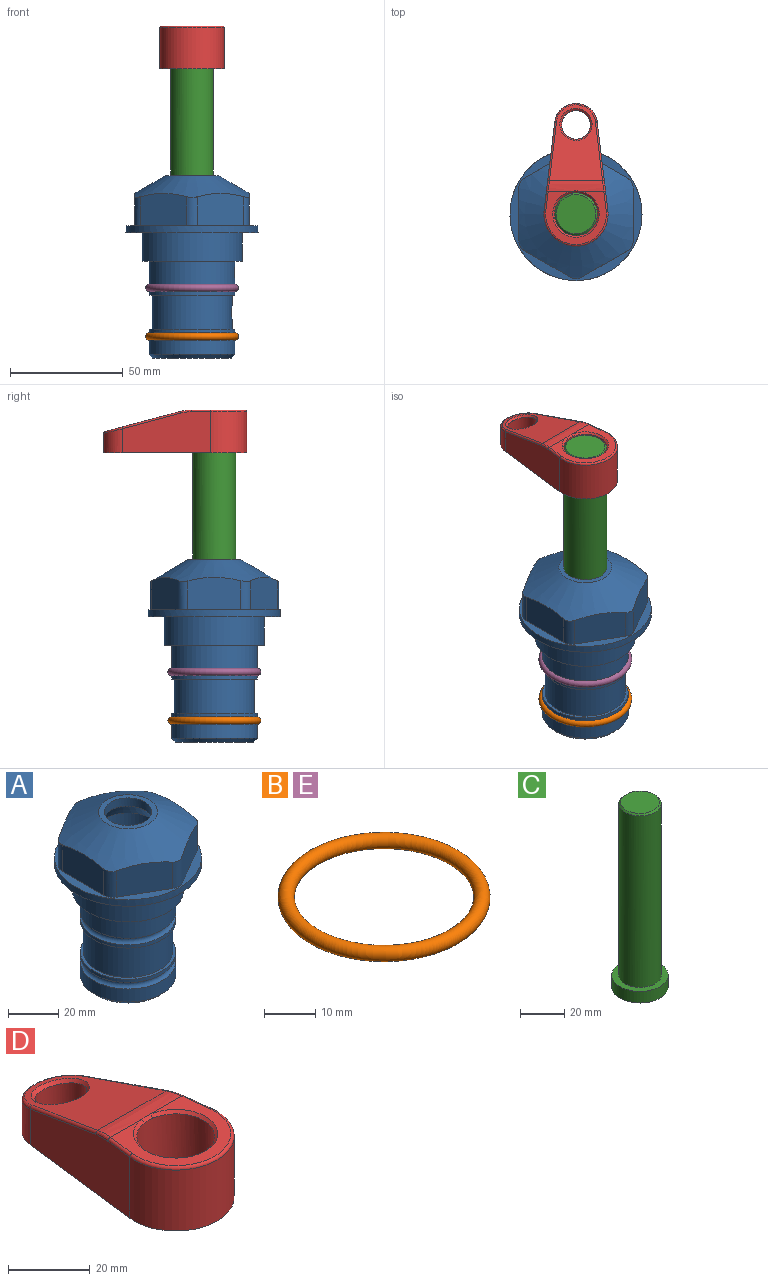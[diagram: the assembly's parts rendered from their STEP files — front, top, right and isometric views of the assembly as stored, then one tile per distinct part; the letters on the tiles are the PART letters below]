
ASSEMBLY  parts=5 mates=4
PART A: 36 faces, bbox 58.7x58.7x81 mm
  f0: cylinder r=17.78mm len=35.56mm, axis (0,0,1), area 1670.8mm2, adj f23,f24,f31
  f1: cylinder r=19.05mm len=38.1mm, axis (0,0,1), area 1191.9mm2, adj f26,f27,f30
  f2: plane 58.66x58.66mm, normal (0,0,-1), area 1150.6mm2, adj f3,f28
  f3: cylinder r=29.33mm len=58.66mm, axis (0,0,-1), area 585.1mm2, adj f2,f4
  f4: plane 58.66x58.66mm, normal (0,0,1), area 475.9mm2, adj f3,f5,f6,f7,f8,f9,f10,f11
  f5: plane 20.32x14.34mm, normal (-0.5,0.87,0), area 324.4mm2, adj f4,f15,f16,f17
  f6: plane 20.32x14.34mm, normal (0.5,0.87,0), area 324.4mm2, adj f4,f14,f15,f17
  f7: plane 23.48x14.34mm, normal (1,0,0), area 324.4mm2, adj f4,f13,f14,f17
  f8: plane 20.32x14.34mm, normal (0.5,-0.87,0), area 324.4mm2, adj f4,f12,f13,f17
  f9: plane 20.32x14.34mm, normal (-0.5,-0.87,0), area 324.4mm2, adj f4,f11,f12,f17
  f10: plane 23.48x14.34mm, normal (-1,0,0), area 324.4mm2, adj f4,f11,f16,f17
  f11: cylinder r=5.08mm len=12.85mm, axis (0,0,-1), area 67.2mm2, adj f4,f9,f10,f17
  f12: cylinder r=5.08mm len=12.85mm, axis (0,0,-1), area 67.2mm2, adj f4,f8,f9,f17
  f13: cylinder r=5.08mm len=12.85mm, axis (0,0,-1), area 67.2mm2, adj f4,f7,f8,f17
  f14: cylinder r=5.08mm len=12.85mm, axis (0,0,-1), area 67.2mm2, adj f4,f6,f7,f17
  f15: cylinder r=5.08mm len=12.85mm, axis (0,0,-1), area 67.2mm2, adj f4,f5,f6,f17
  f16: cylinder r=5.08mm len=12.85mm, axis (0,0,-1), area 67.2mm2, adj f4,f5,f10,f17
  f17: cone r=11.73mm half-angle=60deg, axis (0,0,-1), area 2071.8mm2, adj f5,f6,f7,f8,f9,f10,f11,f12
  f18: plane 23.46x23.46mm, normal (0,0,1), area 147.4mm2, adj f17,f35
  f19: plane 34.93x34.93mm, normal (0,0,-1), area 958mm2, adj f29
  f20: cylinder r=19.05mm len=38.1mm, axis (0,0,1), area 760.1mm2, adj f21,f29
  f21: torus R=19.05mm, axis (0,0,1), area 565.3mm2, adj f20,f22
  f22: cylinder r=19.05mm len=38.1mm, axis (0,0,1), area 190mm2, adj f21,f23
  f23: plane 38.1x38.1mm, normal (0,0,1), area 146.9mm2, adj f0,f22
  f24: plane 38.1x38.1mm, normal (0,0,-1), area 146.9mm2, adj f0,f25
  f25: cylinder r=19.05mm len=38.1mm, axis (0,0,1), area 190mm2, adj f24,f26
  f26: torus R=19.05mm, axis (0,0,1), area 565.3mm2, adj f1,f25
  f27: plane 44.45x44.45mm, normal (0,0,-1), area 411.7mm2, adj f1,f28
  f28: cylinder r=22.23mm len=44.45mm, axis (0,0,1), area 1773.5mm2, adj f2,f27
  f29: cone r=19.05mm half-angle=45deg, axis (0,0,1), area 257.5mm2, adj f19,f20
  f30: cylinder r=3.17mm len=6.75mm, axis (-1,0,0), area 128mm2, adj f1,f33
  f31: cylinder r=3.17mm len=6.35mm, axis (-1,0,0), area 102.5mm2, adj f0,f33
  f32: plane 25.4x25.4mm, normal (0,0,1), area 506.7mm2, adj f33
  f33: cylinder r=12.7mm len=66.42mm, axis (0,0,-1), area 5236.2mm2, adj f30,f31,f32,f34
  f34: cone r=9.53mm half-angle=30deg, axis (0,0,-1), area 443.4mm2, adj f33,f35
  f35: cylinder r=9.53mm len=19.05mm, axis (0,0,-1), area 240.9mm2, adj f18,f34
PART B: 1 faces, bbox 44.7x44.7x3.2 mm
  f0: torus R=19.05mm, axis (0,0,1), area 1193.9mm2
PART C: 6 faces, bbox 25.4x25.4x101.6 mm
  f0: plane 17.46x17.46mm, normal (0,0,1), area 239.5mm2, adj f5
  f1: plane 25.4x25.4mm, normal (0,0,-1), area 506.7mm2, adj f2
  f2: cylinder r=12.7mm len=25.4mm, axis (0,0,1), area 506.7mm2, adj f1,f3
  f3: plane 25.4x25.4mm, normal (0,0,1), area 221.7mm2, adj f2,f4
  f4: cylinder r=9.53mm len=94.46mm, axis (0,0,1), area 5653mm2, adj f3,f5
  f5: cone r=8.73mm half-angle=45deg, axis (0,0,-1), area 64.4mm2, adj f0,f4
PART D: 31 faces, bbox 31.7x65.5x19.8 mm
  f0: plane 39.12x18.26mm, normal (0.99,0.12,0), area 612.2mm2, adj f1,f4,f7,f11,f13,f15
  f1: cylinder r=9.53mm len=18.91mm, axis (0,0,-1), area 296.1mm2, adj f0,f2,f7,f17
  f2: plane 39.12x18.26mm, normal (-0.99,0.12,0), area 612.2mm2, adj f1,f4,f7,f12,f14,f16
  f3: cylinder r=6.35mm len=12.7mm, axis (0,0,-1), area 362.4mm2, adj f7,f18
  f4: cylinder r=14.29mm len=28.58mm, axis (0,0,-1), area 882.2mm2, adj f0,f2,f7,f10
  f5: cylinder r=9.53mm len=19.05mm, axis (0,0,-1), area 1092.6mm2, adj f7,f19,f20
  f6: plane 26.99x23.69mm, normal (0,0,1), area 216.2mm2, adj f9,f10,f11,f12,f19
  f7: plane 63.5x28.58mm, normal (0,0,-1), area 661.8mm2, adj f0,f1,f2,f3,f4,f5,f22,f23
  f8: plane 33.52x23.6mm, normal (0,0.26,0.97), area 486mm2, adj f9,f15,f16,f17,f18
  f9: cylinder r=19.05mm len=24.72mm, axis (1,0,0), area 120.4mm2, adj f6,f8,f13,f14,f20
  f10: torus R=13.49mm, axis (0,0,1), area 59mm2, adj f4,f6,f11,f12
  f11: cylinder r=0.79mm len=8.67mm, axis (0.12,-0.99,0), area 10.8mm2, adj f0,f6,f10,f13
  f12: cylinder r=0.79mm len=8.67mm, axis (0.12,0.99,0), area 10.8mm2, adj f2,f6,f10,f14
  f13: bspline ~4.95x1.42mm, area 6.1mm2, adj f0,f9,f11,f15
  f14: bspline ~4.95x1.42mm, area 6.1mm2, adj f2,f9,f12,f16
  f15: cylinder r=0.79mm len=25.95mm, axis (0.12,-0.96,0.26), area 32.9mm2, adj f0,f8,f13,f17
  f16: cylinder r=0.79mm len=25.95mm, axis (0.12,0.96,-0.26), area 32.9mm2, adj f2,f8,f14,f17
  f17: bspline ~18.91x8.38mm, area 30mm2, adj f1,f8,f15,f16
  f18: bspline ~14.29x14.29mm, area 48.3mm2, adj f3,f8
  f19: cone r=9.53mm half-angle=45deg, axis (0,0,1), area 66.5mm2, adj f5,f6,f20
  f20: bspline ~3.22x0.96mm, area 3.5mm2, adj f5,f9,f19
  f21: plane 2.75x2.72mm, normal (0,0,-1), area 2.9mm2, adj f23,f25,f28
  f22: plane 23.05x15.88mm, normal (-0.99,-0.12,0), area 323.6mm2, adj f7,f25,f26,f27,f28,f29
  f23: plane 23.05x15.88mm, normal (0.99,-0.12,0), area 323.6mm2, adj f7,f21,f25,f27,f28,f30
  f24: cylinder r=9.53mm len=10.69mm, axis (0,0,-1), area 114.7mm2, adj f7,f27,f29,f30
  f25: cylinder r=12.7mm len=20.59mm, axis (0,0,-1), area 381.1mm2, adj f7,f21,f22,f23,f26,f28
  f26: plane 2.75x2.72mm, normal (0,0,-1), area 2.9mm2, adj f22,f25,f28
  f27: plane 19.72x18.37mm, normal (0,-0.26,-0.97), area 291.8mm2, adj f22,f23,f24,f28,f29,f30
  f28: cylinder r=15.88mm len=19.92mm, axis (1,0,0), area 54.8mm2, adj f21,f22,f23,f25,f26,f27
  f29: cylinder r=1.59mm len=11mm, axis (0,0,-1), area 34.7mm2, adj f7,f22,f24,f27
  f30: cylinder r=1.59mm len=11mm, axis (0,0,-1), area 34.7mm2, adj f7,f23,f24,f27
PART E: same geometry as B
PLACE A at identity fixed
PLACE B t=(0,0,-21.59)mm
PLACE C t=(0,0,27.55)mm
PLACE D t=(0,0,28.35)mm
PLACE E at identity
MATE slider C.f2 <-> A.f0  axis (0,0,-1) through (0,0,-10.55)mm
MATE fastened E.f0 <-> A.f0  axis (0,0,1) through (0,0,-24.51)mm
MATE fastened C.f2 <-> D.f4  axis (0,0,1) through (0,0,91.05)mm
MATE fastened B.f0 <-> A.f0  axis (0,0,1) through (0,0,-46.1)mm
